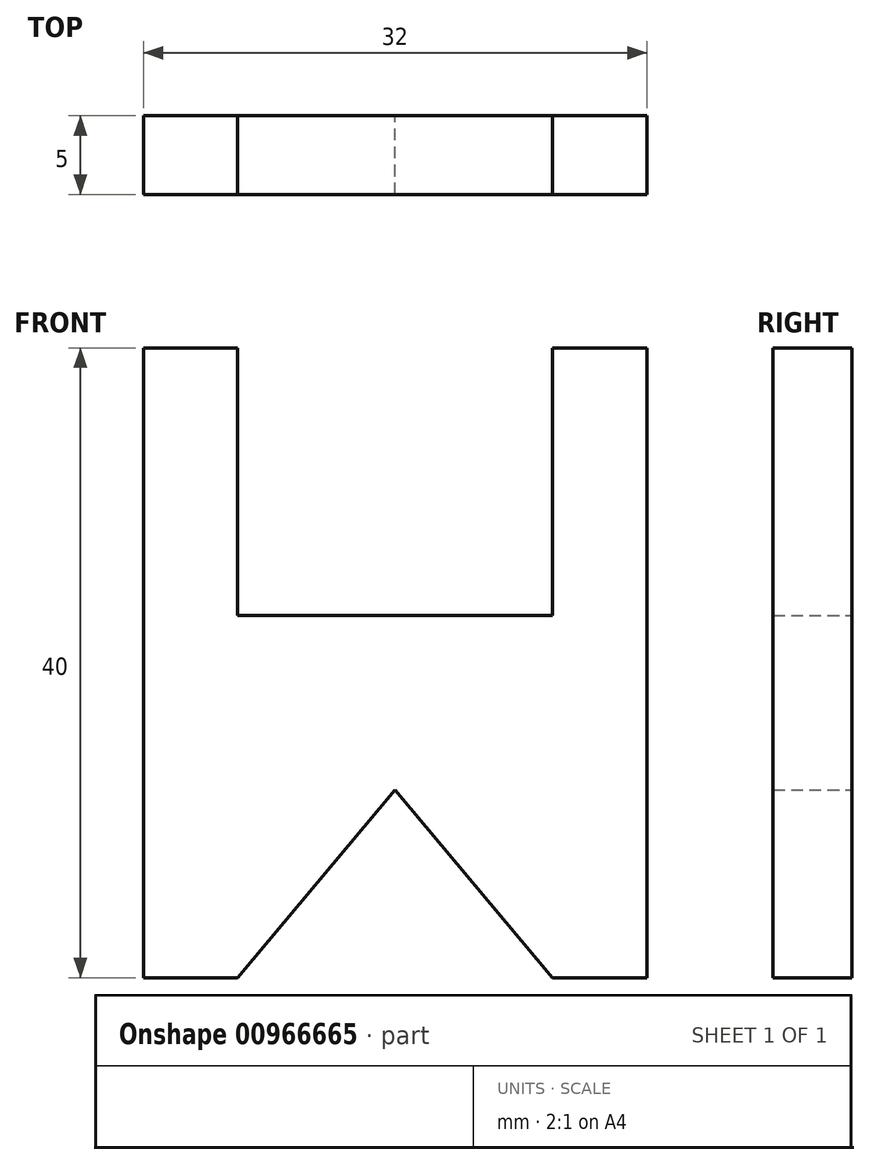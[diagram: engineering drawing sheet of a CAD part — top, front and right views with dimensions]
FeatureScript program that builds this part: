
annotation { "Feature Type Name" : "Feature", "Feature Type Description" : "" }
export const myFeature = defineFeature(function(context is Context, id is Id, definition is map)
    precondition{}
    {
        {
            var Q0;
            Q0=qCreatedBy(makeId("Front.planeOp"),FACE);
            var sketch = newSketch(context, id + "F0", { "sketchPlane" : qUnion([Q0])});
            skLineSegment(sketch, "E0", {"start": v(-16, -20) * mm, "end": v(-10, -20) * mm});
            skLineSegment(sketch, "E1.MirrorCS", {"start": v(-16, 20) * mm, "end": v(-10, 20) * mm});
            skLineSegment(sketch, "E2.MirrorCS", {"start": v(-10, 3) * mm, "end": v(0, 3) * mm});
            skLineSegment(sketch, "E3.MirrorCS", {"start": v(-10, 20) * mm, "end": v(-10, 3) * mm});
            skLineSegment(sketch, "E4.MirrorCS", {"start": v(-16, 0) * mm, "end": v(-16, 20) * mm});
            skLineSegment(sketch, "E5", {"start": v(-16, 0) * mm, "end": v(-16, -20) * mm});
            skLineSegment(sketch, "E6.MirrorCS", {"start": v(16, 20) * mm, "end": v(10, 20) * mm});
            skLineSegment(sketch, "E7.MirrorCS", {"start": v(10, 20) * mm, "end": v(10, 3) * mm});
            skLineSegment(sketch, "E8.MirrorCS", {"start": v(16, -20) * mm, "end": v(10, -20) * mm});
            skLineSegment(sketch, "E9.MirrorCS", {"start": v(16, 0) * mm, "end": v(16, -20) * mm});
            skLineSegment(sketch, "E10.MirrorCS", {"start": v(10, 3) * mm, "end": v(0, 3) * mm});
            skLineSegment(sketch, "E11.MirrorCS", {"start": v(16, 0) * mm, "end": v(16, 20) * mm});
            skLineSegment(sketch, "E12", {"start": v(0, -8.08) * mm, "end": v(-10, -20) * mm});
            skLineSegment(sketch, "E13.MirrorCS", {"start": v(0, -8.08) * mm, "end": v(10, -20) * mm});
            skSolve(sketch);
        }
        {
            var Q0;
            Q0=makeQuery(id+"F0.imprint","IMPRINT",FACE,{"disambiguationData":[TD([[makeQuery(id+"F0.imprint","IMPRINT",EDGE,{"derivedFrom":sQuery(id+"F0.wireOp",EDGE,"E0")}),1.0]])]});
            extrude(context, id + "F1", {"entities" : qUnion([Q0]), "depth" : 5 * mm, "offsetDistance" : 25 * mm});
        }
    });
